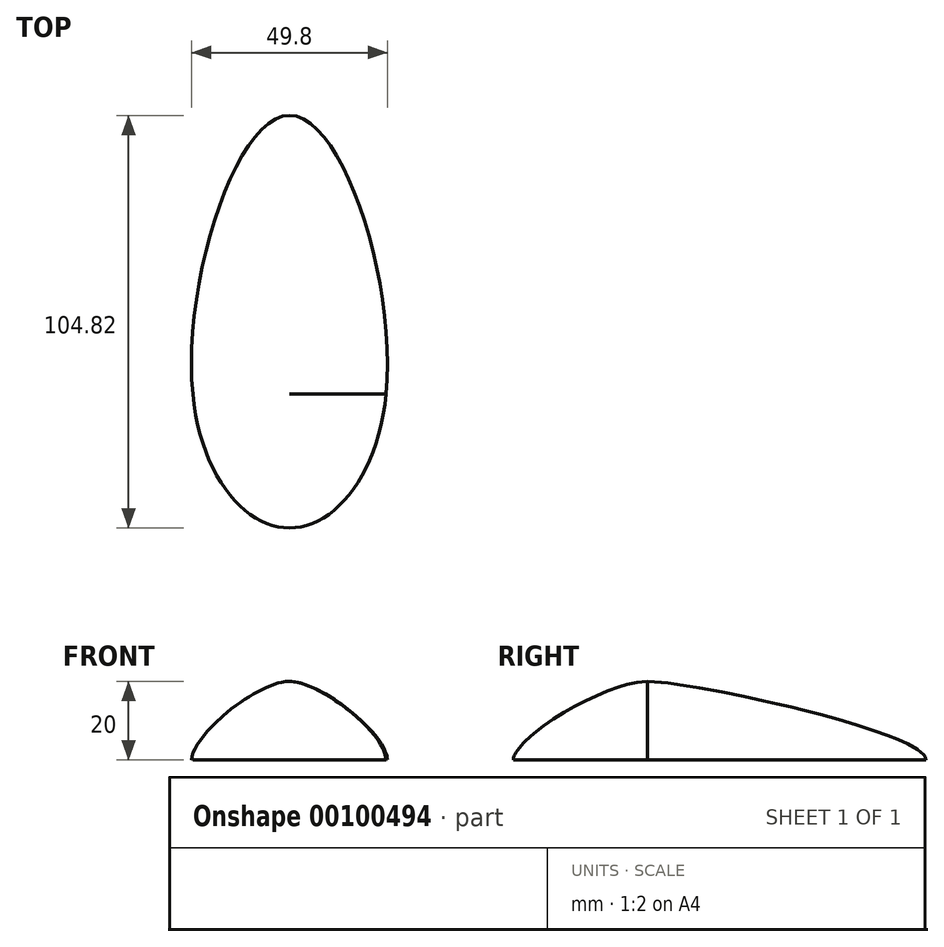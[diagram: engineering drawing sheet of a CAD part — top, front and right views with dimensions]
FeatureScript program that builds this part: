
annotation { "Feature Type Name" : "Feature", "Feature Type Description" : "" }
export const myFeature = defineFeature(function(context is Context, id is Id, definition is map)
    precondition{}
    {
        {
            var Q0;
            Q0=qCreatedBy(makeId("Top.planeOp"),FACE);
            var sketch = newSketch(context, id + "F0", { "sketchPlane" : qUnion([Q0])});
            skLineSegment(sketch, "E0", {"start": v(0, 0) * mm, "end": v(0, -34) * mm, "construction": true});
            skLineSegment(sketch, "E1", {"start": v(0, 0) * mm, "end": v(0, 70.81) * mm, "construction": true});
            skLineSegment(sketch, "E2", {"start": v(0, 0) * mm, "end": v(-24.54, 0) * mm, "construction": true});
            skLineSegment(sketch, "E3", {"start": v(0, 0) * mm, "end": v(24.54, 0) * mm, "construction": true});
            skFitSpline(sketch, "E4", {"points": [v(0, 70.81) * mm, v(-24.54, 0) * mm, v(0, -34) * mm, v(24.54, 0) * mm, v(0, 70.81) * mm]});
            skSolve(sketch);
        }
        {
            var Q0;
            Q0=qCreatedBy(makeId("Front.planeOp"),FACE);
            var sketch = newSketch(context, id + "F1", { "sketchPlane" : qUnion([Q0])});
            skLineSegment(sketch, "E5", {"start": v(0, 0) * mm, "end": v(0, 20) * mm});
            skSolve(sketch);
        }
        {
            var Q0;
            Q0=qCreatedBy(makeId("Right.planeOp"),FACE);
            var sketch = newSketch(context, id + "F2", { "sketchPlane" : qUnion([Q0])});
            skFitSpline(sketch, "E6", {"points": [v(70.81, 0) * mm, v(0, 20) * mm], "startDerivative": vector(0, 22) * mm, "endDerivative": vector(-32.54, 0) * mm});
            skLineSegment(sketch, "E7", {"start": v(10.85, 20) * mm, "end": v(0, 20) * mm, "construction": true});
            skLineSegment(sketch, "E8", {"start": v(70.81, 7.33) * mm, "end": v(70.81, 0) * mm, "construction": true});
            skFitSpline(sketch, "E9", {"points": [v(0, 20) * mm, v(-34, 0) * mm], "startDerivative": vector(-31.74, 0) * mm, "endDerivative": vector(0, -17.45) * mm});
            skSolve(sketch);
        }
        {
            var Q0;
            Q0=qCreatedBy(makeId("Front.planeOp"),FACE);
            var sketch = newSketch(context, id + "F3", { "sketchPlane" : qUnion([Q0])});
            skFitSpline(sketch, "E10", {"points": [v(-24.54, 0) * mm, v(0, 20) * mm], "startDerivative": vector(0, 19.7) * mm, "endDerivative": vector(24.36, 0) * mm});
            skFitSpline(sketch, "E11", {"points": [v(0, 20) * mm, v(24.54, 0) * mm], "startDerivative": vector(23.65, 0) * mm, "endDerivative": vector(0, -20.34) * mm});
            skSolve(sketch);
        }
        {
            var Q0;
            Q0=makeQuery(id+"F0.imprint","IMPRINT",FACE,{"disambiguationData":[TD([[makeQuery(id+"F0.imprint","IMPRINT",EDGE,{"derivedFrom":sQuery(id+"F0.wireOp",EDGE,"E4")}),1.0]])]});
            var Q1;
            Q1=sQuery(id+"F2.wireOp",VERTEX,"E9.0.internal");
            var Q2;
            Q2=sQuery(id+"F2.wireOp",EDGE,"E6");
            var Q3;
            Q3=sQuery(id+"F2.wireOp",EDGE,"E9");
            var Q4;
            Q4=sQuery(id+"F3.wireOp",EDGE,"E10");
            var Q5;
            Q5=sQuery(id+"F3.wireOp",EDGE,"E11");
            loft(context, id + "F4", {"addGuides" : true, "sheetProfilesArray" : [{ "sheetProfileEntities" : qUnion([Q0]) }, { "sheetProfileEntities" : qUnion([Q1]) }], "guidesArray" : [{ "guideEntities" : qUnion([Q2]), "guideDerivativeType" : LoftGuideDerivativeType.DEFAULT, "guideDerivativeMagnitude" : 1 }, { "guideEntities" : qUnion([Q3]), "guideDerivativeType" : LoftGuideDerivativeType.DEFAULT, "guideDerivativeMagnitude" : 1 }, { "guideEntities" : qUnion([Q4]), "guideDerivativeType" : LoftGuideDerivativeType.DEFAULT, "guideDerivativeMagnitude" : 1 }, { "guideEntities" : qUnion([Q5]), "guideDerivativeType" : LoftGuideDerivativeType.DEFAULT, "guideDerivativeMagnitude" : 1 }]});
        }
    });
